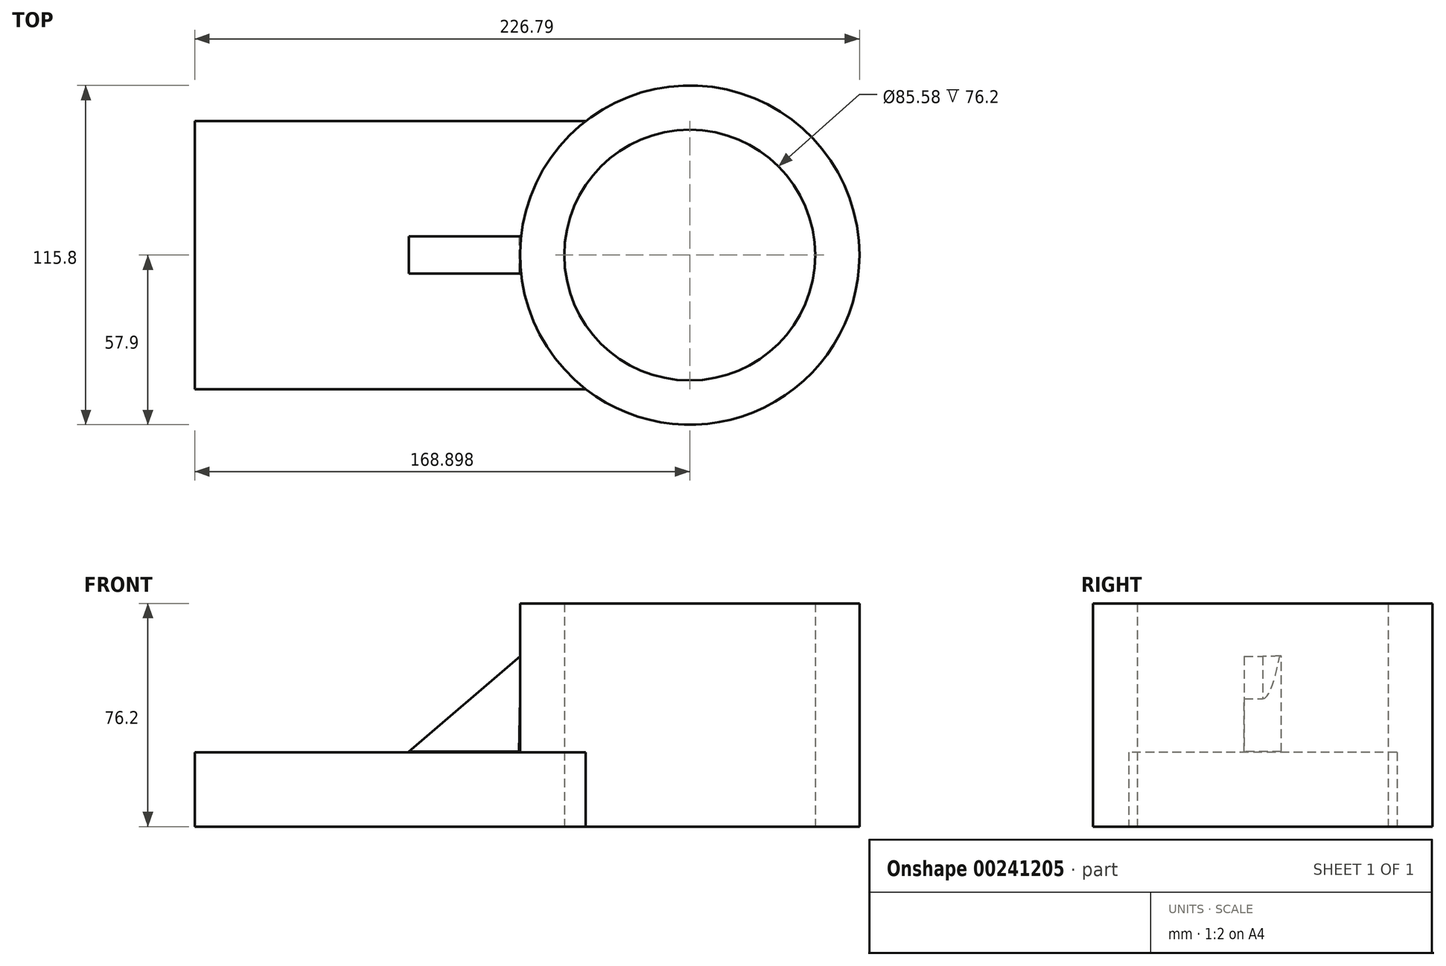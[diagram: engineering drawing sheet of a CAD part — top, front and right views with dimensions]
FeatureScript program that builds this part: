
annotation { "Feature Type Name" : "Feature", "Feature Type Description" : "" }
export const myFeature = defineFeature(function(context is Context, id is Id, definition is map)
    precondition{}
    {
        {
            var Q0;
            Q0=qCreatedBy(makeId("Top.planeOp"),FACE);
            var sketch = newSketch(context, id + "F0", { "sketchPlane" : qUnion([Q0])});
            skLineSegment(sketch, "E0.bottom", {"start": v(49, 45.77) * mm, "end": v(-84.45, 45.77) * mm});
            skLineSegment(sketch, "E0.top", {"start": v(49, -45.77) * mm, "end": v(-84.45, -45.77) * mm});
            skLineSegment(sketch, "E0.right", {"start": v(-84.45, 45.77) * mm, "end": v(-84.45, -45.77) * mm});
            skPoint(sketch, "E0.middle", {"position": v(0, 0) * mm});
            skCircle(sketch, "E1", {"center": v(84.45, 0) * mm, "radius": 57.9 * mm});
            skPoint(sketch, "E2.orphan", {"position": v(84.45, -45.77) * mm});
            skPoint(sketch, "E3.orphan", {"position": v(84.45, 45.77) * mm});
            skCircle(sketch, "E4", {"center": v(84.45, 0) * mm, "radius": 42.79 * mm});
            skSolve(sketch);
        }
        {
            var Q0;
            Q0=makeQuery(id+"F0.imprint","IMPRINT",FACE,{"disambiguationData":[TD([[makeQuery(id+"F0.imprint","IMPRINT",EDGE,{"derivedFrom":sQuery(id+"F0.wireOp",EDGE,"E4")}),-1.0]])]});
            extrude(context, id + "F1", {"entities" : qUnion([Q0]), "depth" : 76.2 * mm});
        }
        {
            var Q0;
            Q0 = qSketchRegion(id + "F0", true);
            extrude(context, id + "F2", {"entities" : qUnion([Q0]), "operationType" : NewBodyOperationType.ADD, "depth" : 25.4 * mm});
        }
        {
            var Q0;
            Q0=qCreatedBy(makeId("Front.planeOp"),FACE);
            var sketch = newSketch(context, id + "F3", { "sketchPlane" : qUnion([Q0])});
            skLineSegment(sketch, "E5", {"start": v(26.84, 58.3) * mm, "end": v(-11.38, 25.6) * mm});
            skLineSegment(sketch, "E6", {"start": v(-11.38, 25.6) * mm, "end": v(26.2, 25.6) * mm});
            skLineSegment(sketch, "E7", {"start": v(26.2, 25.6) * mm, "end": v(26.84, 58.3) * mm});
            skSolve(sketch);
        }
        {
            var Q0;
            Q0=makeQuery(id+"F3.imprint","IMPRINT",FACE,{"disambiguationData":[TD([[makeQuery(id+"F3.imprint","IMPRINT",EDGE,{"derivedFrom":sQuery(id+"F3.wireOp",EDGE,"E5")}),1.0]])]});
            extrude(context, id + "F4", {"entities" : qUnion([Q0]), "operationType" : NewBodyOperationType.ADD, "oppositeDirection" : true, "depth" : 6.35 * mm});
        }
        {
            var Q0;
            Q0=makeQuery(id+"F4.opExtrude","CAP_FACE",FACE,{"disambiguationData":[OSD([sQuery(id+"F3.wireOp",EDGE,"E5"),sQuery(id+"F3.wireOp",EDGE,"E6"),sQuery(id+"F3.wireOp",EDGE,"E7")])],"isStart":true});
            extrude(context, id + "F5", {"entities" : qUnion([Q0]), "operationType" : NewBodyOperationType.ADD, "depth" : 6.35 * mm});
        }
    });
